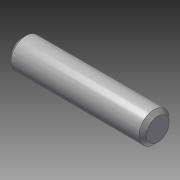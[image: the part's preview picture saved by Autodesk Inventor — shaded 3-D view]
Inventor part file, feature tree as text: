
AUTODESK INVENTOR PART (.ipt)
format: ipt  version: 2014 SP1 (Build 180222100, 222)  size: 76,800 bytes
history: native  units: in
note: dims shown in document units (in); Inventor stores cm internally (conversion verified against a paired STEP export)
features: chamfer x1, other x1, imported_body x1
ambient origin geometry x8: Origin, YZ Plane, XZ Plane, XY Plane, X Axis, Y Axis, Z Axis, Center Point
bodies: Body1 (feature_tree)
feature tree (3):
  chamfer  "Chamfer1"  [1 undecoded]
  other  "PINL-0250-1125-S.ipt1"
  imported_body  "Base1"
note: 1 required parameter value undecoded (feature->parameter linkage not recoverable at this tier; creation-order binding heuristic only, values carry confidence <= 0.55)
